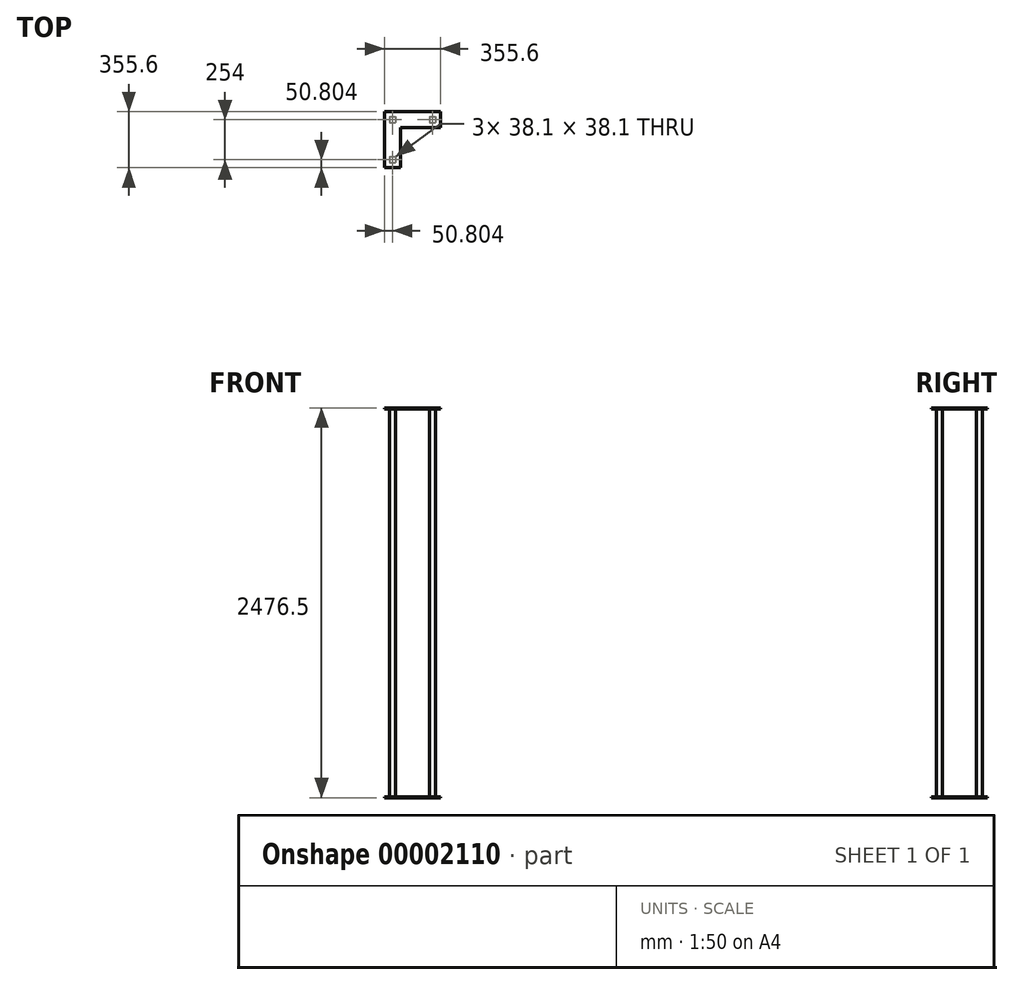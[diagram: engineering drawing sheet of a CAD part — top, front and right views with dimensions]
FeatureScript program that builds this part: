
annotation { "Feature Type Name" : "Feature", "Feature Type Description" : "" }
export const myFeature = defineFeature(function(context is Context, id is Id, definition is map)
    precondition{}
    {
        {
            var Q0;
            Q0=qCreatedBy(makeId("Top.planeOp"),FACE);
            var sketch = newSketch(context, id + "F0", { "sketchPlane" : qUnion([Q0])});
            skLineSegment(sketch, "E0", {"start": v(-169.23, -154.8) * mm, "end": v(-169.23, 200.8) * mm});
            skLineSegment(sketch, "E1", {"start": v(-169.23, 200.8) * mm, "end": v(186.37, 200.8) * mm});
            skLineSegment(sketch, "E2", {"start": v(186.37, 200.8) * mm, "end": v(186.37, 99.2) * mm});
            skLineSegment(sketch, "E3", {"start": v(186.37, 99.2) * mm, "end": v(-67.63, 99.2) * mm});
            skLineSegment(sketch, "E4", {"start": v(-169.23, -154.8) * mm, "end": v(-67.63, -154.8) * mm});
            skLineSegment(sketch, "E5", {"start": v(-67.63, -154.8) * mm, "end": v(-67.63, 99.2) * mm});
            skSolve(sketch);
        }
        {
            var Q0;
            Q0=makeQuery(id+"F0.imprint","IMPRINT",FACE,{"disambiguationData":[TD([[makeQuery(id+"F0.imprint","IMPRINT",EDGE,{"derivedFrom":sQuery(id+"F0.wireOp",EDGE,"E0")}),-1.0]])]});
            extrude(context, id + "F1", {"entities" : qUnion([Q0]), "depth" : 6.35 * mm});
        }
        {
            var Q0;
            Q0=makeQuery(id+"F1.opExtrude","CAP_FACE",FACE,{"disambiguationData":[OSD([sQuery(id+"F0.wireOp",EDGE,"E0"),sQuery(id+"F0.wireOp",EDGE,"E1"),sQuery(id+"F0.wireOp",EDGE,"E2"),sQuery(id+"F0.wireOp",EDGE,"E3"),sQuery(id+"F0.wireOp",EDGE,"E4"),sQuery(id+"F0.wireOp",EDGE,"E5")])],"isStart":false});
            var sketch = newSketch(context, id + "F2", { "sketchPlane" : qUnion([Q0])});
            skSolve(sketch);
        }
        {
            var Q0;
            Q0=makeQuery(id+"F2.imprint","IMPRINT",FACE,{"disambiguationData":[TD([[makeQuery(id+"F2.imprint","IMPRINT",EDGE,{"derivedFrom":makeQuery(id+"F1.opExtrude","CAP_EDGE",EDGE,{"disambiguationData":[OSD([sQuery(id+"F0.wireOp",EDGE,"E0")])],"isStart":false})}),-1.0]])]});
            var sketch = newSketch(context, id + "F3", { "sketchPlane" : qUnion([Q0])});
            skLineSegment(sketch, "E6.bottom", {"start": v(-137.48, -84.95) * mm, "end": v(-99.38, -84.95) * mm});
            skLineSegment(sketch, "E6.top", {"start": v(-137.48, -123.05) * mm, "end": v(-99.38, -123.05) * mm});
            skLineSegment(sketch, "E6.left", {"start": v(-137.48, -84.95) * mm, "end": v(-137.48, -123.05) * mm});
            skLineSegment(sketch, "E6.right", {"start": v(-99.38, -84.95) * mm, "end": v(-99.38, -123.05) * mm});
            skLineSegment(sketch, "E7.bottom", {"start": v(-137.48, 169.05) * mm, "end": v(-99.38, 169.05) * mm});
            skLineSegment(sketch, "E7.top", {"start": v(-137.48, 130.95) * mm, "end": v(-99.38, 130.95) * mm});
            skLineSegment(sketch, "E7.left", {"start": v(-137.48, 169.05) * mm, "end": v(-137.48, 130.95) * mm});
            skLineSegment(sketch, "E7.right", {"start": v(-99.38, 169.05) * mm, "end": v(-99.38, 130.95) * mm});
            skLineSegment(sketch, "E8.bottom", {"start": v(116.52, 169.05) * mm, "end": v(154.62, 169.05) * mm});
            skLineSegment(sketch, "E8.top", {"start": v(116.52, 130.95) * mm, "end": v(154.62, 130.95) * mm});
            skLineSegment(sketch, "E8.left", {"start": v(116.52, 169.05) * mm, "end": v(116.52, 130.95) * mm});
            skLineSegment(sketch, "E8.right", {"start": v(154.62, 169.05) * mm, "end": v(154.62, 130.95) * mm});
            skSolve(sketch);
        }
        {
            var Q0;
            Q0 = qSketchRegion(id + "F3", true);
            extrude(context, id + "F4", {"entities" : qUnion([Q0]), "operationType" : NewBodyOperationType.ADD, "depth" : 2463.8 * mm});
        }
        {
            var Q0;
            Q0=makeQuery(id+"F4.opExtrude","CAP_FACE",FACE,{"disambiguationData":[OSD([sQuery(id+"F3.wireOp",EDGE,"E6.bottom"),sQuery(id+"F3.wireOp",EDGE,"E6.top"),sQuery(id+"F3.wireOp",EDGE,"E6.left"),sQuery(id+"F3.wireOp",EDGE,"E6.right")])],"isStart":false});
            cPlane(context, id + "F5", {"entities" : qUnion([Q0]), "cplaneType" : CPlaneType.OFFSET, "offset" : 0 * mm, "width" : 152.4 * mm, "height" : 152.4 * mm});
        }
        {
            var Q0;
            Q0=qCreatedBy(id+"F5.planeOp",FACE);
            var sketch = newSketch(context, id + "F6", { "sketchPlane" : qUnion([Q0])});
            skLineSegment(sketch, "E9", {"start": v(-169.23, -154.8) * mm, "end": v(-169.23, 200.8) * mm});
            skLineSegment(sketch, "E10", {"start": v(-169.23, 200.8) * mm, "end": v(186.37, 200.8) * mm});
            skLineSegment(sketch, "E11", {"start": v(186.37, 200.8) * mm, "end": v(186.37, 99.2) * mm});
            skLineSegment(sketch, "E12", {"start": v(186.37, 99.2) * mm, "end": v(-67.63, 99.2) * mm});
            skLineSegment(sketch, "E13", {"start": v(-67.63, 99.2) * mm, "end": v(-67.63, -154.8) * mm});
            skLineSegment(sketch, "E14", {"start": v(-67.63, -154.8) * mm, "end": v(-169.23, -154.8) * mm});
            skSolve(sketch);
        }
        {
            var Q0;
            Q0 = qSketchRegion(id + "F6", true);
            extrude(context, id + "F7", {"entities" : qUnion([Q0]), "operationType" : NewBodyOperationType.ADD, "depth" : 6.35 * mm});
        }
    });
